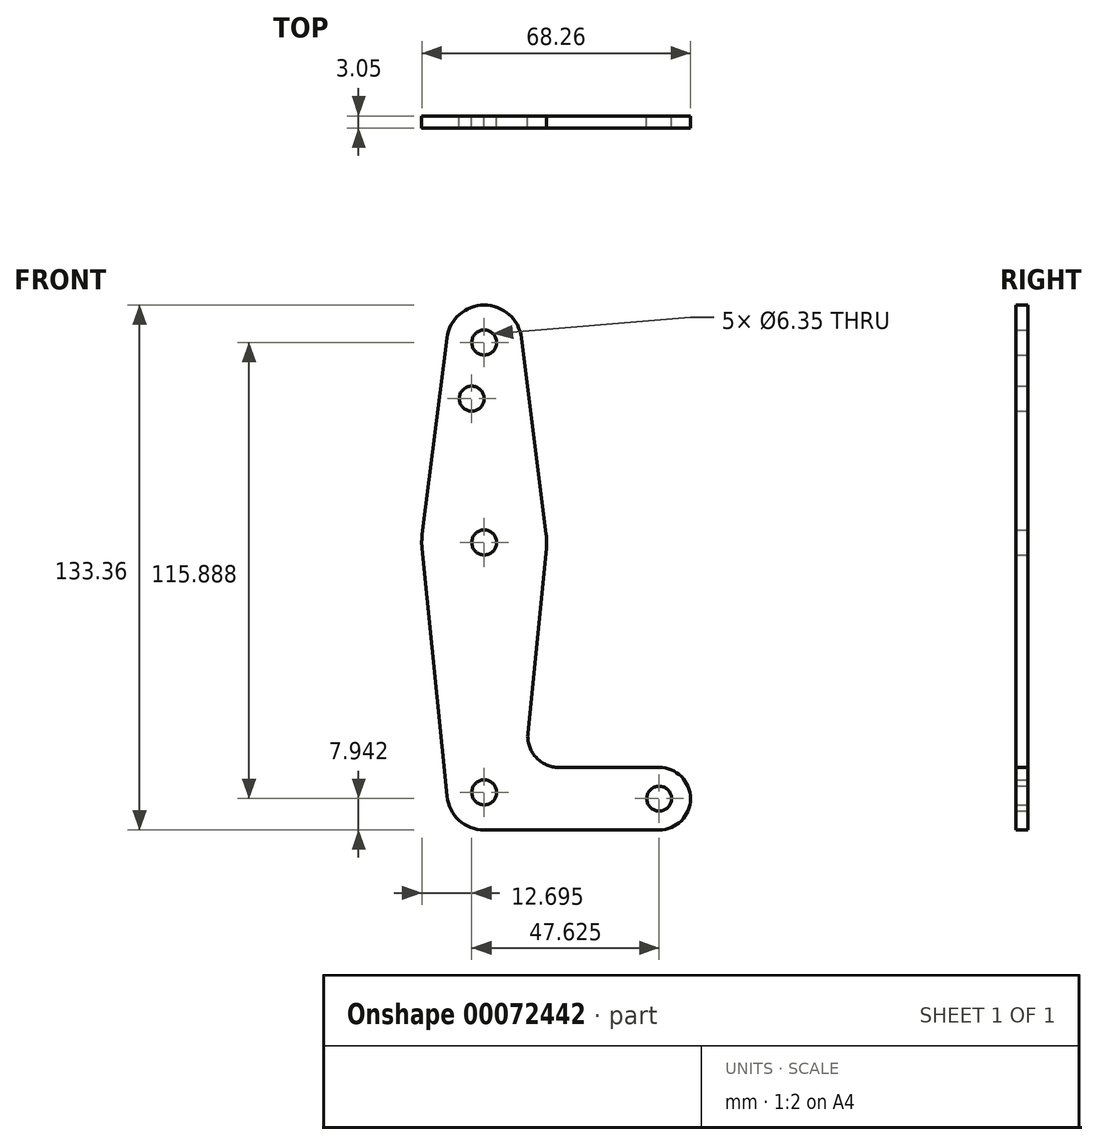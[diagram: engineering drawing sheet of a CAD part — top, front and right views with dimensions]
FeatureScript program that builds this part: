
annotation { "Feature Type Name" : "Feature", "Feature Type Description" : "" }
export const myFeature = defineFeature(function(context is Context, id is Id, definition is map)
    precondition{}
    {
        {
            var Q0;
            Q0=qCreatedBy(makeId("Front.planeOp"),FACE);
            var sketch = newSketch(context, id + "F0", { "sketchPlane" : qUnion([Q0])});
            skCircle(sketch, "E0", {"center": v(0, 114.3) * mm, "radius": 9.53 * mm});
            skCircle(sketch, "E1", {"center": v(0, 63.5) * mm, "radius": 15.88 * mm});
            skCircle(sketch, "E2", {"center": v(0, 0) * mm, "radius": 9.53 * mm});
            skCircle(sketch, "E3", {"center": v(44.45, -1.59) * mm, "radius": 7.94 * mm});
            skLineSegment(sketch, "E4", {"start": v(-9.45, 115.5) * mm, "end": v(-15.75, 65.48) * mm});
            skLineSegment(sketch, "E5", {"start": v(9.45, 115.5) * mm, "end": v(15.75, 65.48) * mm});
            skLineSegment(sketch, "E6", {"start": v(-15.8, 61.91) * mm, "end": v(-9.48, -0.95) * mm});
            skLineSegment(sketch, "E7", {"start": v(15.8, 61.91) * mm, "end": v(11.1, 15.1) * mm});
            skLineSegment(sketch, "E8", {"start": v(19, 6.35) * mm, "end": v(44.45, 6.35) * mm});
            skLineSegment(sketch, "E9", {"start": v(0, -9.52) * mm, "end": v(44.45, -9.53) * mm});
            skCircle(sketch, "E10", {"center": v(0, 114.3) * mm, "radius": 3.18 * mm});
            skCircle(sketch, "E11", {"center": v(0, 63.5) * mm, "radius": 3.18 * mm});
            skCircle(sketch, "E12", {"center": v(0, 0) * mm, "radius": 3.18 * mm});
            skCircle(sketch, "E13", {"center": v(44.45, -1.59) * mm, "radius": 3.18 * mm});
            skArc(sketch, "E14.filletArc", {"start": v(11.1, 15.1) * mm, "mid": v(13.1, 8.97) * mm, "end": v(19, 6.35) * mm});
            skCircle(sketch, "E15", {"center": v(-3.18, 100.03) * mm, "radius": 3.18 * mm});
            skLineSegment(sketch, "E16", {"start": v(0, 114.3) * mm, "end": v(0, 0) * mm, "construction": true});
            skLineSegment(sketch, "E17", {"start": v(0, 0) * mm, "end": v(44.45, -1.59) * mm, "construction": true});
            skSolve(sketch);
        }
        {
            var Q0;
            Q0 = qSketchRegion(id + "F0", true);
            extrude(context, id + "F1", {"entities" : qUnion([Q0]), "depth" : 3.05 * mm});
        }
    });
